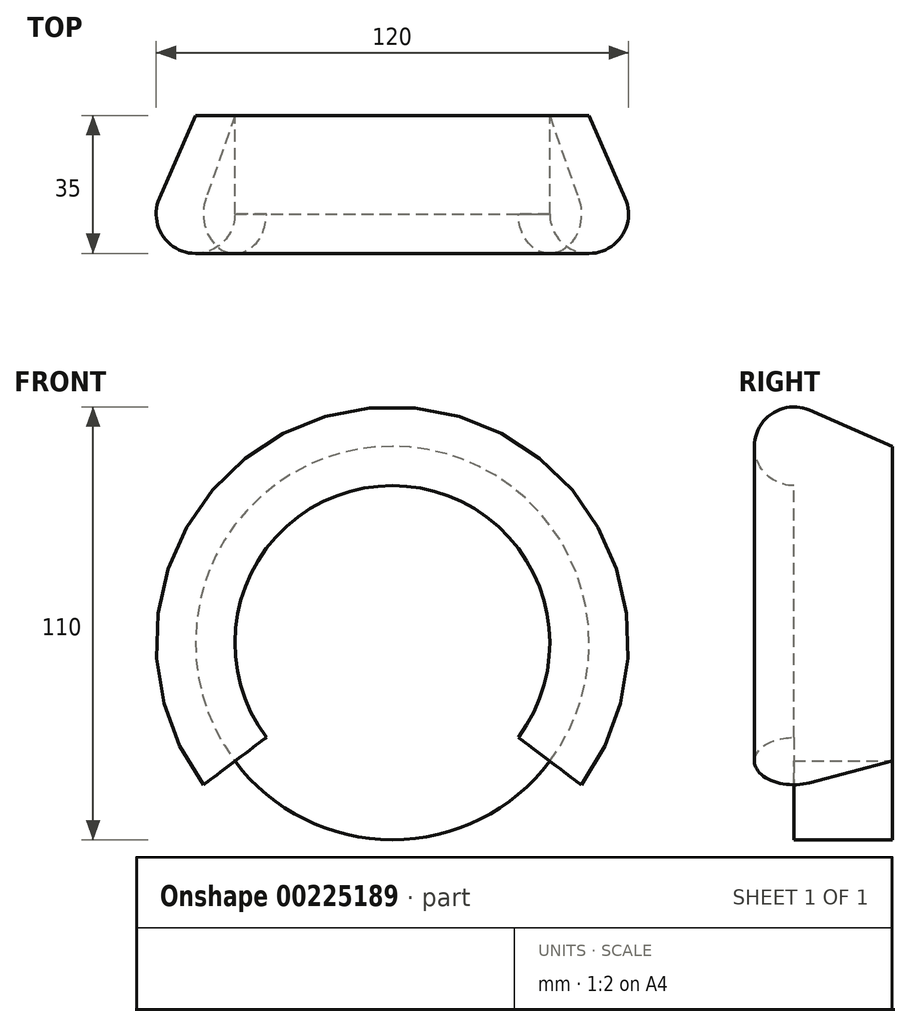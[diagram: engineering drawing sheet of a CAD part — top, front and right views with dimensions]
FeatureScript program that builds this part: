
annotation { "Feature Type Name" : "Feature", "Feature Type Description" : "" }
export const myFeature = defineFeature(function(context is Context, id is Id, definition is map)
    precondition{}
    {
        {
            var Q0;
            Q0=qCreatedBy(makeId("Front.planeOp"),FACE);
            var sketch = newSketch(context, id + "F0", { "sketchPlane" : qUnion([Q0])});
            skCircle(sketch, "E0", {"center": v(0, 0) * mm, "radius": 50 * mm});
            skSolve(sketch);
        }
        {
            var Q0;
            Q0 = qSketchRegion(id + "F0", true);
            extrude(context, id + "F1", {"entities" : qUnion([Q0]), "endBound" : BoundingType.SYMMETRIC, "depth" : 25 * mm});
        }
        {
            var Q0;
            Q0=makeQuery(id+"F1.opExtrude","CAP_FACE",FACE,{"disambiguationData":[OSD([sQuery(id+"F0.wireOp",EDGE,"E0")])],"isStart":false});
            var sketch = newSketch(context, id + "F2", { "sketchPlane" : qUnion([Q0])});
            skArc(sketch, "E1", {"start": v(40, -30) * mm, "mid": v(0, 50) * mm, "end": v(-40, -30) * mm});
            skLineSegment(sketch, "E2", {"start": v(-40, -30) * mm, "end": v(40, -30) * mm, "construction": true});
            skLineSegment(sketch, "E3", {"start": v(-40, -30) * mm, "end": v(-21.5, -16.13) * mm, "construction": true});
            skLineSegment(sketch, "E4", {"start": v(-40, -30) * mm, "end": v(-16.07, -61.9) * mm, "construction": true});
            skSolve(sketch);
        }
        {
            var Q0;
            Q0=sQuery(id+"F2.wireOp",EDGE,"E3");
            cPlane(context, id + "F3", {"entities" : qUnion([Q0]), "cplaneType" : CPlaneType.LINE_ANGLE, "offset" : 25 * mm, "angle" : 90 * degree, "width" : 150 * mm, "height" : 150 * mm});
        }
        {
            var Q0;
            Q0=qCreatedBy(id+"F3.planeOp",FACE);
            var sketch = newSketch(context, id + "F4", { "sketchPlane" : qUnion([Q0])});
            skArc(sketch, "E5", {"start": v(-59.17, -8.5) * mm, "mid": v(-44.52, -20.87) * mm, "end": v(-50, -2.5) * mm});
            skLineSegment(sketch, "E6", {"start": v(-50, 12.5) * mm, "end": v(-59.17, -8.5) * mm});
            skLineSegment(sketch, "E7", {"start": v(-50, -12.5) * mm, "end": v(-50, 13.31) * mm, "construction": true});
            skLineSegment(sketch, "E8", {"start": v(-50, -2.5) * mm, "end": v(-50, 12.5) * mm});
            skSolve(sketch);
        }
        {
            var Q0;
            Q0=makeQuery(id+"F4.imprint","IMPRINT",FACE,{"disambiguationData":[TD([[makeQuery(id+"F4.imprint","IMPRINT",EDGE,{"derivedFrom":sQuery(id+"F4.wireOp",EDGE,"E5")}),1.0]])]});
            var Q1;
            Q1=sQuery(id+"F2.wireOp",EDGE,"E1");
            sweep(context, id + "F5", {"operationType" : NewBodyOperationType.ADD, "profiles" : qUnion([Q0]), "path" : qUnion([Q1])});
        }
    });
